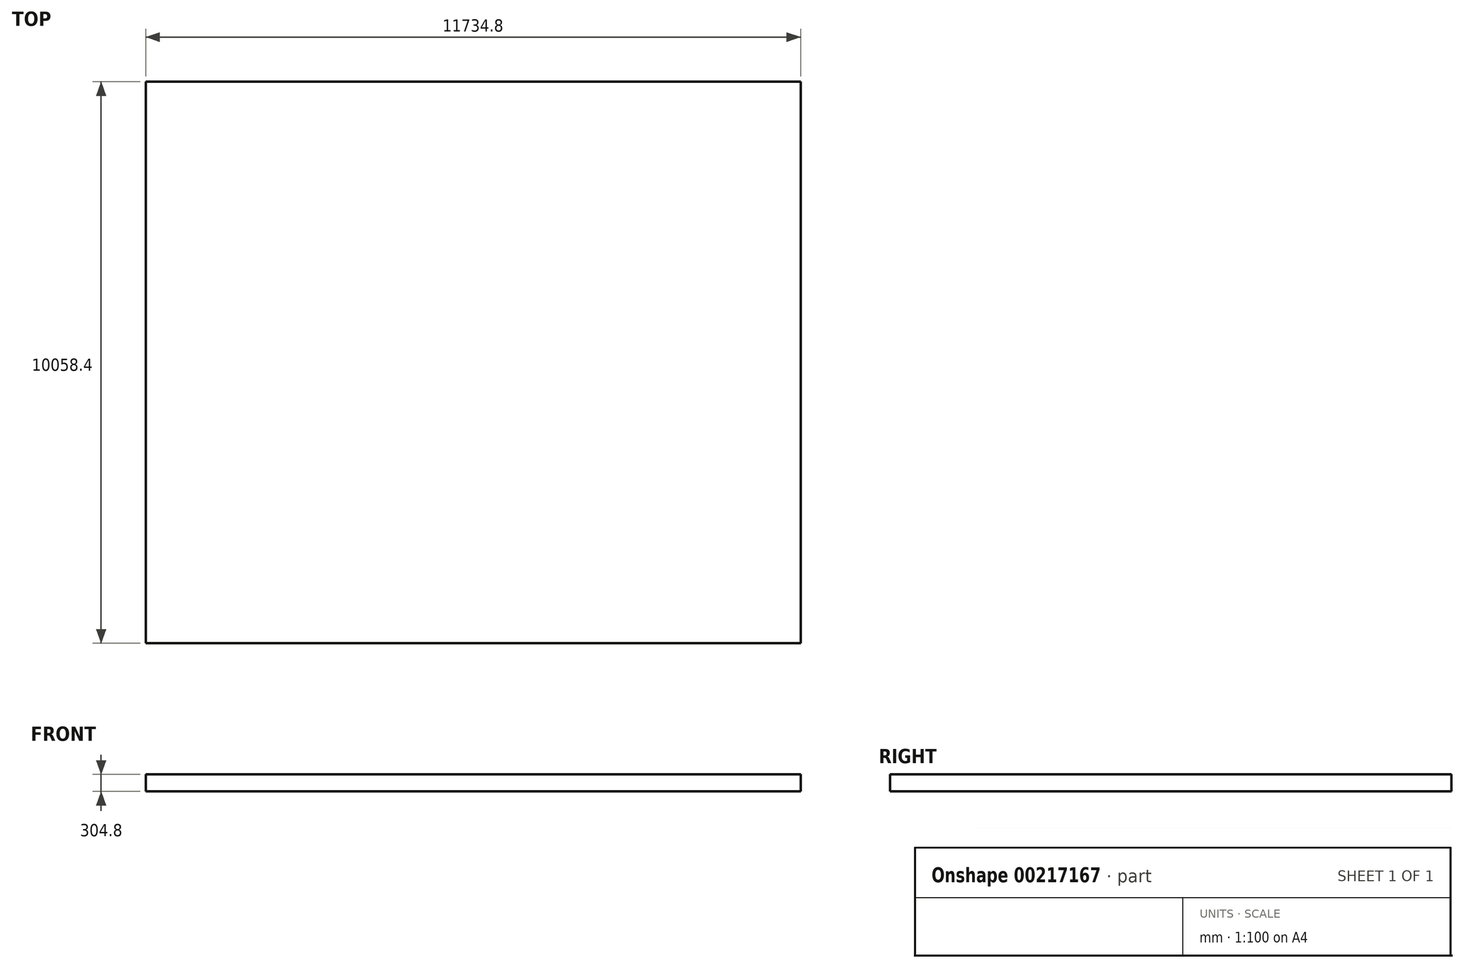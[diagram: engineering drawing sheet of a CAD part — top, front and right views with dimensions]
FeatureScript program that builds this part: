
annotation { "Feature Type Name" : "Feature", "Feature Type Description" : "" }
export const myFeature = defineFeature(function(context is Context, id is Id, definition is map)
    precondition{}
    {
        {
            var Q0;
            Q0=qCreatedBy(makeId("Top.planeOp"),FACE);
            var sketch = newSketch(context, id + "F0", { "sketchPlane" : qUnion([Q0])});
            skLineSegment(sketch, "E0.bottom", {"start": v(0, 0) * mm, "end": v(11734.8, 0) * mm});
            skLineSegment(sketch, "E0.top", {"start": v(0, 10058.4) * mm, "end": v(11734.8, 10058.4) * mm});
            skLineSegment(sketch, "E0.left", {"start": v(0, 0) * mm, "end": v(0, 10058.4) * mm});
            skLineSegment(sketch, "E0.right", {"start": v(11734.8, 0) * mm, "end": v(11734.8, 10058.4) * mm});
            skSolve(sketch);
        }
        {
            var Q0;
            Q0 = qSketchRegion(id + "F0", true);
            extrude(context, id + "F1", {"entities" : qUnion([Q0]), "depth" : 304.8 * mm});
        }
    });
